# Revit family: DRL E Comfort Claudia Elektrisch_EcoDsign 760
name_source: partatom
category: Attrezzatura meccanica
units: mm (PartAtom-declared; Revit-internal decimal feet)

## family parameters
Condiviso = No
Host = Muro
Numero OmniClass = 23.75.00.00
Punto di calcolo locali = Sì
Quota connettore circolare = Usa diametro
Sempre verticale = Sì
Taglio con vuoti quando caricato = No
Tipo di parte = Normale
Titolo OmniClass = Climate Control (HVAC)

## types (6) — shared parameters
Adaptive (self-learning) = Sì
Air exhaust = No
Colour = White RAL9016
Degree of protection (IP) = IP44
Depth = 30 mm  [stored 0.0984252 ft]
Digital indication = Sì
Dist_wall = 40 mm  [stored 0.131234 ft]
Frequency supply voltage = 50 Hz
Front material = Not present
Frost protection circuit = Sì
Height = 760 mm
Material heating element = Steel
Model = Vertical
Mounting direction = Vertical
Mounting method = Wall
Number of switch positions = 5
Oil-/fluid-filled = Yes
Open window detection = Sì
Overheating protection = Sì
Position control panel = Down
Power control = No
Produttore = DRL Products BV
Programmable = Sì
Protection class = I
Supply voltage = 230 V
URL = https://www.drl-products.nl
With decorative finish = No
With presence indicator = No
With timer = Sì
zero-valued in all types: Number of ribs, Number of supported pilot wire commands

## per-type parameters (varying)
| type | Consumption indication | Heating capacity | L_rad | Operation by app | Suitable for bus connection | Suitable for wireless remote control | Weight | Width | With remote control | l_ing |
| Claudia EcoDesign 760x400 400W RAL9016 | No | 400 W | 320 mm  [stored 1.04987 ft] | No | No | No | 0.11 kN | 400 mm  [stored 1.31234 ft] | No | -320 mm  [stored -1.04987 ft] |
| Claudia Elektrisch 760x400 400W RAL9016 | Sì | 400 W | 320 mm  [stored 1.04987 ft] | Sì | Sì | Yes | 0.11 kN | 400 mm  [stored 1.31234 ft] | Yes | -320 mm  [stored -1.04987 ft] |
| Claudia EcoDesign 760x500 500W RAL9016 | No | 500 W | 420 mm  [stored 1.37795 ft] | No | No | No | 0.13 kN | 500 mm  [stored 1.64042 ft] | No | -420 mm  [stored -1.37795 ft] |
| Claudia Electrich 760x500 500W RAL9016 | No | 500 W | 420 mm  [stored 1.37795 ft] | No | No | No | 0.13 kN | 500 mm  [stored 1.64042 ft] | Yes | -420 mm  [stored -1.37795 ft] |
| Claudia Electrich 760x600 600W RAL9016 | No | 600 W | 520 mm  [stored 1.70604 ft] | No | No | No | 0.15 kN | 600 mm | Yes | -520 mm  [stored -1.70604 ft] |
| Claudia EcoDesign 760x600 600W RAL9016 | No | 600 W | 520 mm  [stored 1.70604 ft] | No | No | No | 0.15 kN | 600 mm | No | -520 mm  [stored -1.70604 ft] |

note: [stored X ft] marks values corroborated as IEEE doubles in the binary element streams (Revit-internal decimal feet)
